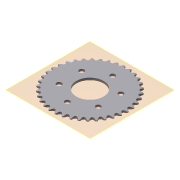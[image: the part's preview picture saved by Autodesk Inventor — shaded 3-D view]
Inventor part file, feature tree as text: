
AUTODESK INVENTOR PART (.ipt)
format: ipt  version: 2011 (Build 150239000, 239)  size: 950,272 bytes
history: native  units: mm
features: other x7, extrude x3, sketch x2, pattern_linear x1, pattern_circular x1, hole x1
ambient origin geometry x8: Origin, YZ Plane, XZ Plane, XY Plane, X Axis, Y Axis, Z Axis, Center Point
bodies: Solid1 (feature_tree)
feature tree (15):
  other  "25 sprocket 38T"
  other  "Theoretical Tooth Profile"
  other  "Tooth Profile"
  other  "Section Profile"
  other  "Shroud"
  other  "Strand"
  pattern_linear  "Strand Pattern"  Spacing1=1.697355mm  [1 undecoded]
  extrude  "Theoretical Tooth"  Depth=22.092194mm
  extrude  "Tooth"  Depth=2.884386mm
  pattern_circular  "Tooth Pattern"  [2 undecoded]
  other  "Timing Plane"
  extrude  "Extrusion4"  Depth=4.338955mm
  hole  "Hole2"  [1 undecoded]
  sketch  "Sketch4"  dims[d0=76.895741mm]
  sketch  "Sketch6"  dims[d2=1.65347mm d3=1.697355mm d10=22.092194mm d11=2.884386mm d12=2.6416mm d13=4.338955mm d14=4.6228mm d18=10.0mm d19=0.0mm d20=380.0mm d21=360.0deg d23=1.905mm d28=0.0mm d29=0.0mm d30=2.286mm d31=64.960832mm d32=2.286mm d33=0.79375mm d34=6.75005mm d36=90.0deg d37=90.0deg d38=10.0mm d40=6.4008mm d42=0.0mm d43=1.143mm d44=23.998278mm d45=1.697355mm d46=15.05712mm d47=0.0mm d48=25.4mm d49=0.0mm d50=10.0mm d52=25.4mm d53=0.0mm d67=28.5623mm d68=47.625mm d69=5.2324mm d70=60.0mm d72=360.0deg d74=5.2324mm d75=19.05mm d76=9.525mm d77=6.35mm d78=14.3117mm d79=25.4mm d80=20.594885mm]
note: 4 required parameter values undecoded (feature->parameter linkage not recoverable at this tier; creation-order binding heuristic only, values carry confidence <= 0.55)
